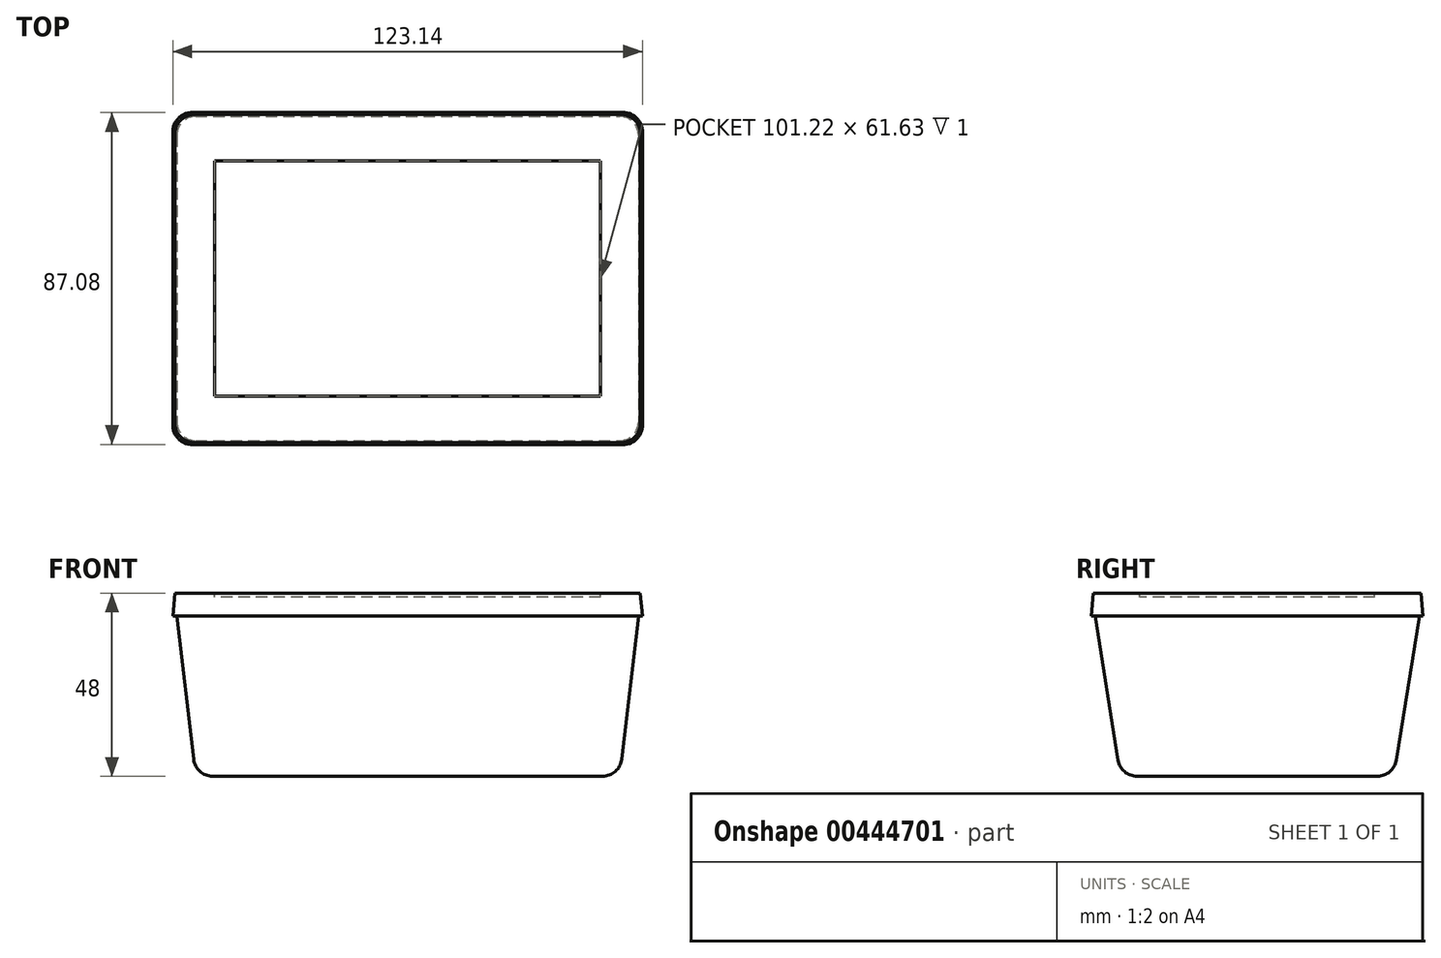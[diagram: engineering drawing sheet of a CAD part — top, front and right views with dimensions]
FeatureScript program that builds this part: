
annotation { "Feature Type Name" : "Feature", "Feature Type Description" : "" }
export const myFeature = defineFeature(function(context is Context, id is Id, definition is map)
    precondition{}
    {
        {
            var Q0;
            Q0=qCreatedBy(makeId("Top.planeOp"),FACE);
            var sketch = newSketch(context, id + "F0", { "sketchPlane" : qUnion([Q0])});
            skLineSegment(sketch, "E0.bottom", {"start": v(55.6, 35.81) * mm, "end": v(-55.6, 35.81) * mm});
            skLineSegment(sketch, "E0.top", {"start": v(55.6, -35.81) * mm, "end": v(-55.6, -35.81) * mm});
            skLineSegment(sketch, "E0.left", {"start": v(55.6, 35.81) * mm, "end": v(55.6, -35.81) * mm});
            skLineSegment(sketch, "E0.right", {"start": v(-55.6, 35.81) * mm, "end": v(-55.6, -35.81) * mm});
            skPoint(sketch, "E0.middle", {"position": v(0, 0) * mm});
            skSolve(sketch);
        }
        {
            var Q0;
            Q0=qCreatedBy(makeId("Top.planeOp"),FACE);
            cPlane(context, id + "F1", {"entities" : qUnion([Q0]), "cplaneType" : CPlaneType.OFFSET, "offset" : 42 * mm, "width" : 150 * mm, "height" : 150 * mm});
        }
        {
            var Q0;
            Q0=qCreatedBy(id+"F1.planeOp",FACE);
            var sketch = newSketch(context, id + "F2", { "sketchPlane" : qUnion([Q0])});
            skLineSegment(sketch, "E1.bottom", {"start": v(-60.57, 42.53) * mm, "end": v(60.57, 42.53) * mm});
            skLineSegment(sketch, "E1.top", {"start": v(-60.57, -42.53) * mm, "end": v(60.57, -42.53) * mm});
            skLineSegment(sketch, "E1.left", {"start": v(-60.57, 42.54) * mm, "end": v(-60.57, -42.53) * mm});
            skLineSegment(sketch, "E1.right", {"start": v(60.57, 42.53) * mm, "end": v(60.57, -42.54) * mm});
            skPoint(sketch, "E1.middle", {"position": v(0, 0) * mm});
            skSolve(sketch);
        }
        {
            var Q0;
            Q0=makeQuery(id+"F0.imprint","IMPRINT",FACE,{"disambiguationData":[TD([[makeQuery(id+"F0.imprint","IMPRINT",EDGE,{"derivedFrom":sQuery(id+"F0.wireOp",EDGE,"E0.bottom")}),1.0]])]});
            var Q1;
            Q1=makeQuery(id+"F2.imprint","IMPRINT",FACE,{"disambiguationData":[TD([[makeQuery(id+"F2.imprint","IMPRINT",EDGE,{"derivedFrom":sQuery(id+"F2.wireOp",EDGE,"E1.bottom")}),-1.0]])]});
            loft(context, id + "F3", {"sheetProfilesArray" : [{ "sheetProfileEntities" : qUnion([Q0]) }, { "sheetProfileEntities" : qUnion([Q1]) }]});
        }
        {
            var Q0;
            Q0=makeQuery(id+"F3.opLoft","SWEPT_EDGE",EDGE,{"disambiguationData":[OSD([sQuery(id+"F0.wireOp",EDGE,"E0.top"),sQuery(id+"F0.wireOp",EDGE,"E0.right"),sQuery(id+"F2.wireOp",EDGE,"E1.top"),sQuery(id+"F2.wireOp",EDGE,"E1.left")])]});
            var Q1;
            Q1=makeQuery(id+"F3.opLoft","MID_CAP_EDGE",EDGE,{"disambiguationData":[OSD([sQuery(id+"F0.wireOp",EDGE,"E0.top"),sQuery(id+"F0.wireOp",EDGE,"E0.left"),sQuery(id+"F0.wireOp",EDGE,"E0.right")])],"capPos":0.0});
            var Q2;
            Q2=makeQuery(id+"F3.opLoft","SWEPT_EDGE",EDGE,{"disambiguationData":[OSD([sQuery(id+"F0.wireOp",EDGE,"E0.top"),sQuery(id+"F0.wireOp",EDGE,"E0.left"),sQuery(id+"F2.wireOp",EDGE,"E1.top"),sQuery(id+"F2.wireOp",EDGE,"E1.right")])]});
            var Q3;
            Q3=makeQuery(id+"F3.opLoft","MID_CAP_EDGE",EDGE,{"disambiguationData":[OSD([sQuery(id+"F0.wireOp",EDGE,"E0.bottom"),sQuery(id+"F0.wireOp",EDGE,"E0.top"),sQuery(id+"F0.wireOp",EDGE,"E0.left")])],"capPos":0.0});
            var Q4;
            Q4=makeQuery(id+"F3.opLoft","SWEPT_EDGE",EDGE,{"disambiguationData":[OSD([sQuery(id+"F0.wireOp",EDGE,"E0.bottom"),sQuery(id+"F0.wireOp",EDGE,"E0.left"),sQuery(id+"F2.wireOp",EDGE,"E1.bottom"),sQuery(id+"F2.wireOp",EDGE,"E1.right")])]});
            var Q5;
            Q5=makeQuery(id+"F3.opLoft","MID_CAP_EDGE",EDGE,{"disambiguationData":[OSD([sQuery(id+"F0.wireOp",EDGE,"E0.bottom"),sQuery(id+"F0.wireOp",EDGE,"E0.left"),sQuery(id+"F0.wireOp",EDGE,"E0.right")])],"capPos":0.0});
            var Q6;
            Q6=makeQuery(id+"F3.opLoft","SWEPT_EDGE",EDGE,{"disambiguationData":[OSD([sQuery(id+"F0.wireOp",EDGE,"E0.bottom"),sQuery(id+"F0.wireOp",EDGE,"E0.right"),sQuery(id+"F2.wireOp",EDGE,"E1.bottom"),sQuery(id+"F2.wireOp",EDGE,"E1.left")])]});
            var Q7;
            Q7=makeQuery(id+"F3.opLoft","MID_CAP_EDGE",EDGE,{"disambiguationData":[OSD([sQuery(id+"F0.wireOp",EDGE,"E0.bottom"),sQuery(id+"F0.wireOp",EDGE,"E0.top"),sQuery(id+"F0.wireOp",EDGE,"E0.right")])],"capPos":0.0});
            fillet(context, id + "F4", {"entities" : qUnion([Q0, Q1, Q2, Q3, Q4, Q5, Q6, Q7]), "radius" : 5 * mm, "tangentPropagation" : true, "allowEdgeOverflow" : false});
        }
        {
            var Q0;
            Q0=makeQuery(id+"F3.opLoft","CAP_FACE",FACE,{"disambiguationData":[OSD([makeQuery(id+"F2.imprint","IMPRINT",FACE,{"disambiguationData":[TD([[makeQuery(id+"F2.imprint","IMPRINT",EDGE,{"derivedFrom":sQuery(id+"F2.wireOp",EDGE,"E1.bottom")}),-1.0]])]})])],"isStart":true});
            cPlane(context, id + "F5", {"entities" : qUnion([Q0]), "cplaneType" : CPlaneType.OFFSET, "offset" : 0 * mm, "width" : 150 * mm, "height" : 150 * mm});
        }
        {
            var Q0;
            Q0=qCreatedBy(id+"F5.planeOp",FACE);
            var sketch = newSketch(context, id + "F6", { "sketchPlane" : qUnion([Q0])});
            skLineSegment(sketch, "E2.bottom", {"start": v(61.57, 43.54) * mm, "end": v(-61.57, 43.54) * mm});
            skLineSegment(sketch, "E2.top", {"start": v(61.57, -43.53) * mm, "end": v(-61.57, -43.53) * mm});
            skLineSegment(sketch, "E2.left", {"start": v(61.57, 43.54) * mm, "end": v(61.57, -43.53) * mm});
            skLineSegment(sketch, "E2.right", {"start": v(-61.57, 43.54) * mm, "end": v(-61.57, -43.53) * mm});
            skPoint(sketch, "E2.middle", {"position": v(0, 0) * mm});
            skSolve(sketch);
        }
        {
            var Q0;
            Q0 = qSketchRegion(id + "F6", true);
            extrude(context, id + "F7", {"entities" : qUnion([Q0]), "operationType" : NewBodyOperationType.ADD, "depth" : 6 * mm});
        }
        {
            var Q0;
            Q0=makeQuery(id+"F7.opExtrude","CAP_EDGE",EDGE,{"disambiguationData":[OSD([sQuery(id+"F6.wireOp",EDGE,"E2.top")])],"isStart":false});
            var Q1;
            Q1=makeQuery(id+"F7.opExtrude","CAP_EDGE",EDGE,{"disambiguationData":[OSD([sQuery(id+"F6.wireOp",EDGE,"E2.right")])],"isStart":false});
            var Q2;
            Q2=makeQuery(id+"F7.opExtrude","CAP_EDGE",EDGE,{"disambiguationData":[OSD([sQuery(id+"F6.wireOp",EDGE,"E2.left")])],"isStart":false});
            var Q3;
            Q3=makeQuery(id+"F7.opExtrude","CAP_EDGE",EDGE,{"disambiguationData":[OSD([sQuery(id+"F6.wireOp",EDGE,"E2.bottom")])],"isStart":false});
            chamfer(context, id + "F8", {"entities" : qUnion([Q0, Q1, Q2, Q3]), "chamferType" : ChamferType.OFFSET_ANGLE, "width" : 6 * mm, "oppositeDirection" : false, "angle" : 5 * degree, "tangentPropagation" : true});
        }
        {
            var Q0;
            Q0=makeQuery(id+"F7.opExtrude","CAP_FACE",FACE,{"disambiguationData":[OSD([sQuery(id+"F6.wireOp",EDGE,"E2.bottom"),sQuery(id+"F6.wireOp",EDGE,"E2.top"),sQuery(id+"F6.wireOp",EDGE,"E2.left"),sQuery(id+"F6.wireOp",EDGE,"E2.right")])],"isStart":false});
            cPlane(context, id + "F9", {"entities" : qUnion([Q0]), "cplaneType" : CPlaneType.OFFSET, "offset" : 0 * mm, "width" : 150 * mm, "height" : 150 * mm});
        }
        {
            var Q0;
            Q0=qCreatedBy(id+"F9.planeOp",FACE);
            var sketch = newSketch(context, id + "F10", { "sketchPlane" : qUnion([Q0])});
            skLineSegment(sketch, "E3.bottom", {"start": v(50.6, 30.82) * mm, "end": v(-50.6, 30.82) * mm});
            skLineSegment(sketch, "E3.top", {"start": v(50.6, -30.82) * mm, "end": v(-50.6, -30.82) * mm});
            skLineSegment(sketch, "E3.left", {"start": v(50.6, 30.82) * mm, "end": v(50.6, -30.82) * mm});
            skLineSegment(sketch, "E3.right", {"start": v(-50.6, 30.82) * mm, "end": v(-50.6, -30.82) * mm});
            skPoint(sketch, "E3.middle", {"position": v(0, 0) * mm});
            skSolve(sketch);
        }
        {
            var Q0;
            Q0=makeQuery(id+"F10.imprint","IMPRINT",FACE,{"disambiguationData":[TD([[makeQuery(id+"F10.imprint","IMPRINT",EDGE,{"derivedFrom":sQuery(id+"F10.wireOp",EDGE,"E3.bottom")}),1.0]])]});
            extrude(context, id + "F11", {"entities" : qUnion([Q0]), "operationType" : NewBodyOperationType.REMOVE, "oppositeDirection" : true, "depth" : 1 * mm});
        }
        {
            var Q0;
            Q0=makeQuery(id+"F8.opChamfer","BLEND_EDGE",EDGE,{"blendedFrom":[makeQuery(id+"F7.opExtrude","CAP_EDGE",EDGE,{"disambiguationData":[OSD([sQuery(id+"F6.wireOp",EDGE,"E2.top")])],"isStart":false}),makeQuery(id+"F7.opExtrude","CAP_EDGE",EDGE,{"disambiguationData":[OSD([sQuery(id+"F6.wireOp",EDGE,"E2.right")])],"isStart":false})],"blendedInto":[]});
            var Q1;
            Q1=makeQuery(id+"F8.opChamfer","BLEND_EDGE",EDGE,{"blendedFrom":[makeQuery(id+"F7.opExtrude","CAP_EDGE",EDGE,{"disambiguationData":[OSD([sQuery(id+"F6.wireOp",EDGE,"E2.top")])],"isStart":false}),makeQuery(id+"F7.opExtrude","CAP_EDGE",EDGE,{"disambiguationData":[OSD([sQuery(id+"F6.wireOp",EDGE,"E2.left")])],"isStart":false})],"blendedInto":[]});
            var Q2;
            Q2=makeQuery(id+"F8.opChamfer","BLEND_EDGE",EDGE,{"blendedFrom":[makeQuery(id+"F7.opExtrude","CAP_EDGE",EDGE,{"disambiguationData":[OSD([sQuery(id+"F6.wireOp",EDGE,"E2.bottom")])],"isStart":false}),makeQuery(id+"F7.opExtrude","CAP_EDGE",EDGE,{"disambiguationData":[OSD([sQuery(id+"F6.wireOp",EDGE,"E2.left")])],"isStart":false})],"blendedInto":[]});
            var Q3;
            Q3=makeQuery(id+"F8.opChamfer","BLEND_EDGE",EDGE,{"blendedFrom":[makeQuery(id+"F7.opExtrude","CAP_EDGE",EDGE,{"disambiguationData":[OSD([sQuery(id+"F6.wireOp",EDGE,"E2.bottom")])],"isStart":false}),makeQuery(id+"F7.opExtrude","CAP_EDGE",EDGE,{"disambiguationData":[OSD([sQuery(id+"F6.wireOp",EDGE,"E2.right")])],"isStart":false})],"blendedInto":[]});
            fillet(context, id + "F12", {"entities" : qUnion([Q0, Q1, Q2, Q3]), "radius" : 5 * mm, "tangentPropagation" : true, "allowEdgeOverflow" : false});
        }
    });
